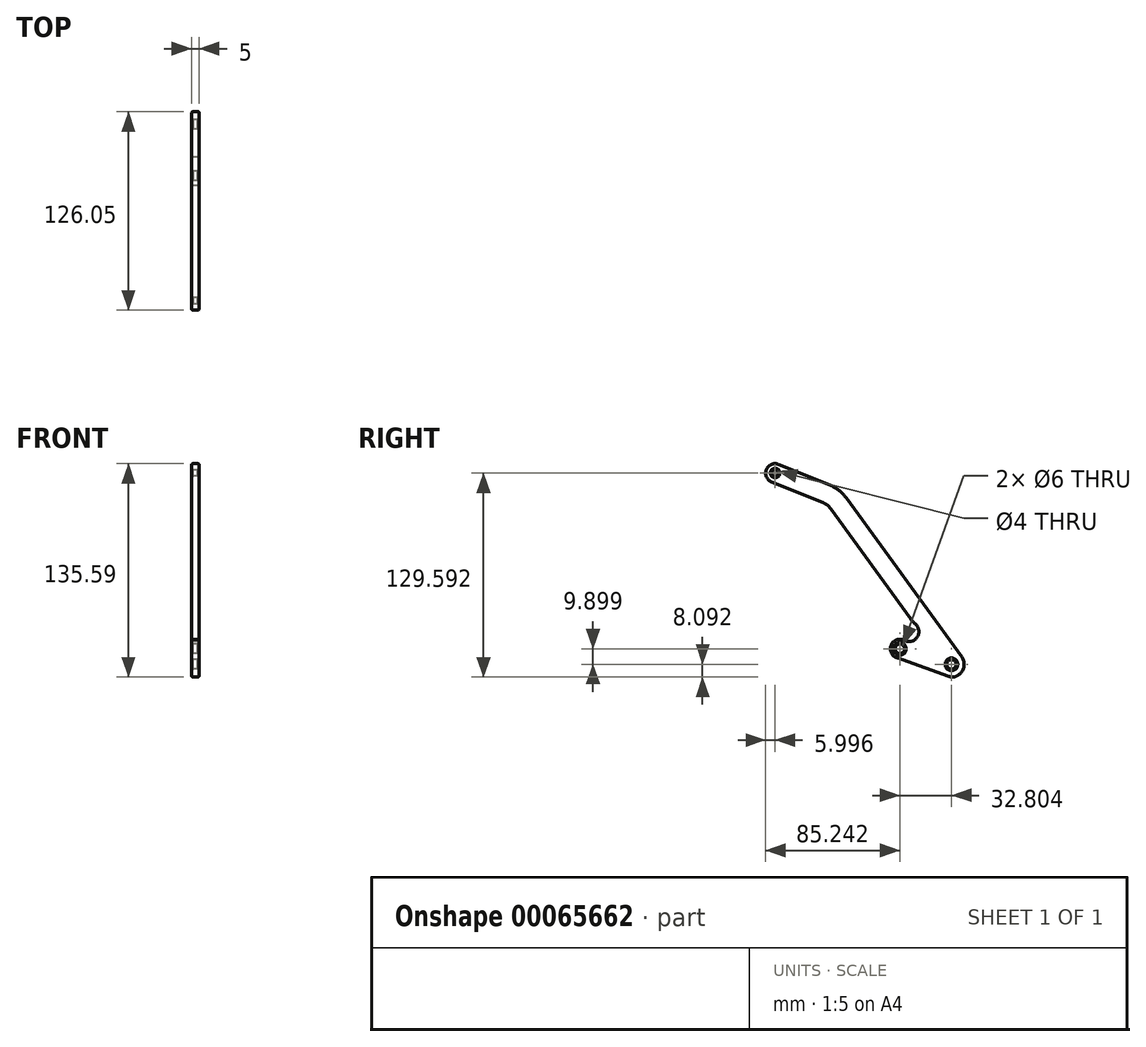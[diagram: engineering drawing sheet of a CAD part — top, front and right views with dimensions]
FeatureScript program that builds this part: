
annotation { "Feature Type Name" : "Feature", "Feature Type Description" : "" }
export const myFeature = defineFeature(function(context is Context, id is Id, definition is map)
    precondition{}
    {
        {
            var Q0;
            Q0=qCreatedBy(makeId("Right.planeOp"),FACE);
            var sketch = newSketch(context, id + "F0", { "sketchPlane" : qUnion([Q0])});
            skLineSegment(sketch, "E0", {"start": v(59.5, -49.27) * mm, "end": v(-13.85, 51.76) * mm});
            skLineSegment(sketch, "E1", {"start": v(-24.25, 59.9) * mm, "end": v(-56.77, 73.1) * mm});
            skPoint(sketch, "E2.visualSharp", {"position": v(-17.88, 57.32) * mm});
            skArc(sketch, "E2.filletArc", {"start": v(-13.85, 51.76) * mm, "mid": v(-18.48, 56.56) * mm, "end": v(-24.25, 59.9) * mm});
            skLineSegment(sketch, "E3.0", {"start": v(-28.76, 48.78) * mm, "end": v(-61.28, 61.97) * mm});
            skArc(sketch, "E3.1", {"start": v(-23.56, 44.71) * mm, "mid": v(-25.87, 47.11) * mm, "end": v(-28.76, 48.78) * mm});
            skLineSegment(sketch, "E3.2", {"start": v(26.9, -24.8) * mm, "end": v(-23.56, 44.71) * mm});
            skArc(sketch, "E4", {"start": v(-56.77, 73.1) * mm, "mid": v(-64.58, 69.79) * mm, "end": v(-61.28, 61.97) * mm});
            skLineSegment(sketch, "E5", {"start": v(57.73, -60.44) * mm, "end": v(57.08, -60.91) * mm});
            skLineSegment(sketch, "E6", {"start": v(51.49, -61.7) * mm, "end": v(21.5, -50.71) * mm});
            skArc(sketch, "E7", {"start": v(23.02, -38.76) * mm, "mid": v(31.15, -36.8) * mm, "end": v(30.22, -28.49) * mm});
            skArc(sketch, "E8", {"start": v(23.02, -38.76) * mm, "mid": v(14.6, -41.95) * mm, "end": v(18.83, -49.9) * mm});
            skPoint(sketch, "E9.visualSharp", {"position": v(19.68, -50.05) * mm});
            skArc(sketch, "E9.filletArc", {"start": v(21.5, -50.71) * mm, "mid": v(20.18, -50.27) * mm, "end": v(18.83, -49.9) * mm});
            skPoint(sketch, "E10.visualSharp", {"position": v(28.93, -27.58) * mm});
            skArc(sketch, "E10.filletArc", {"start": v(26.9, -24.8) * mm, "mid": v(28.46, -26.73) * mm, "end": v(30.22, -28.49) * mm});
            skPoint(sketch, "E11.visualSharp", {"position": v(64.2, -55.74) * mm});
            skArc(sketch, "E11.filletArc", {"start": v(57.73, -60.44) * mm, "mid": v(60.93, -55.22) * mm, "end": v(59.5, -49.27) * mm});
            skPoint(sketch, "E12.visualSharp", {"position": v(54.49, -62.8) * mm});
            skArc(sketch, "E12.filletArc", {"start": v(51.49, -61.7) * mm, "mid": v(54.38, -62) * mm, "end": v(57.08, -60.91) * mm});
            skCircle(sketch, "E13", {"center": v(53.03, -53.97) * mm, "radius": 3 * mm});
            skCircle(sketch, "E14", {"center": v(20.22, -44.07) * mm, "radius": 3 * mm});
            skCircle(sketch, "E15", {"center": v(-59.02, 67.53) * mm, "radius": 2 * mm});
            skSolve(sketch);
        }
        {
            var Q0;
            Q0=makeQuery(id+"F0.imprint","IMPRINT",FACE,{"disambiguationData":[TD([[makeQuery(id+"F0.imprint","IMPRINT",EDGE,{"derivedFrom":sQuery(id+"F0.wireOp",EDGE,"E0")}),1.0]])]});
            extrude(context, id + "F1", {"entities" : qUnion([Q0]), "depth" : 5 * mm});
        }
        {
            var Q0;
            Q0=makeQuery(id+"F1.opExtrude","CAP_EDGE",EDGE,{"disambiguationData":[OSD([sQuery(id+"F0.wireOp",EDGE,"E1")])],"isStart":true});
            var Q1;
            Q1=makeQuery(id+"F1.opExtrude","CAP_EDGE",EDGE,{"disambiguationData":[OSD([sQuery(id+"F0.wireOp",EDGE,"E1")])],"isStart":false});
            fillet(context, id + "F2", {"entities" : qUnion([Q0, Q1]), "radius" : 1 * mm, "tangentPropagation" : true, "allowEdgeOverflow" : false});
        }
        {
            var Q0;
            Q0=makeQuery(id+"F1.opExtrude","CAP_EDGE",EDGE,{"disambiguationData":[OSD([sQuery(id+"F0.wireOp",EDGE,"E14")])],"isStart":false});
            var Q1;
            Q1=makeQuery(id+"F1.opExtrude","CAP_EDGE",EDGE,{"disambiguationData":[OSD([sQuery(id+"F0.wireOp",EDGE,"E14")])],"isStart":true});
            var Q2;
            Q2=makeQuery(id+"F1.opExtrude","CAP_EDGE",EDGE,{"disambiguationData":[OSD([sQuery(id+"F0.wireOp",EDGE,"E13")])],"isStart":false});
            var Q3;
            Q3=makeQuery(id+"F1.opExtrude","CAP_EDGE",EDGE,{"disambiguationData":[OSD([sQuery(id+"F0.wireOp",EDGE,"E13")])],"isStart":true});
            var Q4;
            Q4=makeQuery(id+"F1.opExtrude","CAP_EDGE",EDGE,{"disambiguationData":[OSD([sQuery(id+"F0.wireOp",EDGE,"E15")])],"isStart":true});
            var Q5;
            Q5=makeQuery(id+"F1.opExtrude","CAP_EDGE",EDGE,{"disambiguationData":[OSD([sQuery(id+"F0.wireOp",EDGE,"E15")])],"isStart":false});
            chamfer(context, id + "F3", {"entities" : qUnion([Q0, Q1, Q2, Q3, Q4, Q5]), "width" : 1 * mm, "tangentPropagation" : true});
        }
    });
